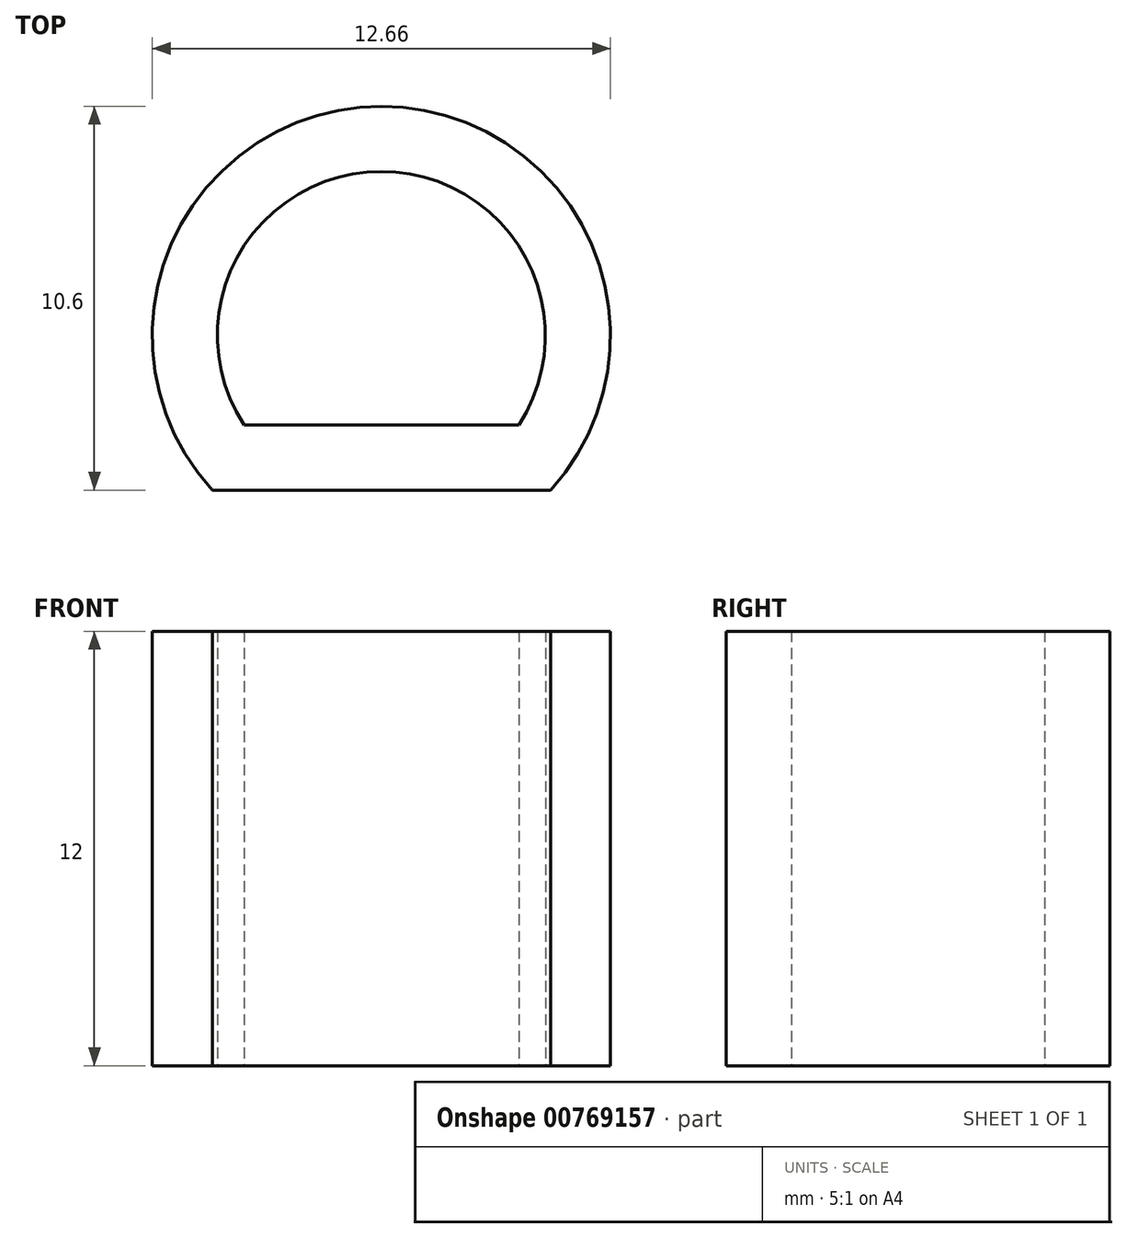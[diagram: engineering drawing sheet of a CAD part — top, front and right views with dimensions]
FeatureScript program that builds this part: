
annotation { "Feature Type Name" : "Feature", "Feature Type Description" : "" }
export const myFeature = defineFeature(function(context is Context, id is Id, definition is map)
    precondition{}
    {
        {
            var Q0;
            Q0=qCreatedBy(makeId("Top.planeOp"),FACE);
            var sketch = newSketch(context, id + "F0", { "sketchPlane" : qUnion([Q0])});
            skLineSegment(sketch, "E0", {"start": v(-3.8, 0.12) * mm, "end": v(3.8, 0.12) * mm});
            skArc(sketch, "E1", {"start": v(3.8, 0.12) * mm, "mid": v(0, 7.12) * mm, "end": v(-3.8, 0.12) * mm});
            skLineSegment(sketch, "E2", {"start": v(-2.45, 7.12) * mm, "end": v(2.15, 7.12) * mm, "construction": true});
            skArc(sketch, "E3.0", {"start": v(4.68, -1.68) * mm, "mid": v(0, 8.92) * mm, "end": v(-4.68, -1.68) * mm});
            skLineSegment(sketch, "E3.1", {"start": v(-4.68, -1.68) * mm, "end": v(4.68, -1.68) * mm});
            skLineSegment(sketch, "E4", {"start": v(-4.53, 8.91) * mm, "end": v(-4.53, -3.91) * mm, "construction": true});
            skLineSegment(sketch, "E5", {"start": v(0, -2.96) * mm, "end": v(0, 12.04) * mm, "construction": true});
            skSolve(sketch);
        }
        {
            var Q0;
            Q0=makeQuery(id+"F0.imprint","IMPRINT",FACE,{"disambiguationData":[TD([[makeQuery(id+"F0.imprint","IMPRINT",EDGE,{"derivedFrom":sQuery(id+"F0.wireOp",EDGE,"E0")}),-1.0]])]});
            extrude(context, id + "F1", {"entities" : qUnion([Q0]), "depth" : 12 * mm, "offsetDistance" : 25 * mm});
        }
    });
